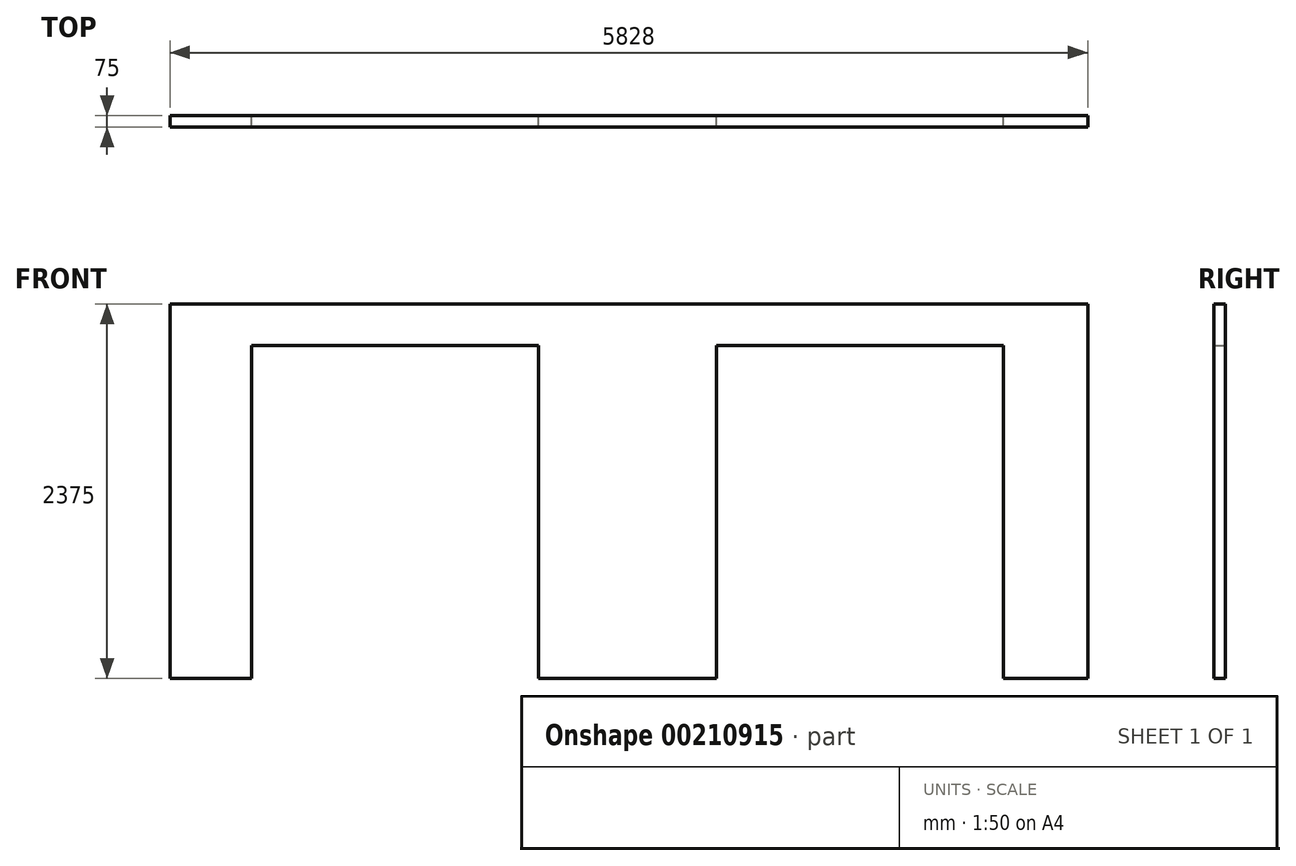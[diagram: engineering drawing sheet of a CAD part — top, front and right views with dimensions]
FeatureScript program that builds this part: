
annotation { "Feature Type Name" : "Feature", "Feature Type Description" : "" }
export const myFeature = defineFeature(function(context is Context, id is Id, definition is map)
    precondition{}
    {
        {
            var Q0;
            Q0=qCreatedBy(makeId("Front.planeOp"),FACE);
            var sketch = newSketch(context, id + "F0", { "sketchPlane" : qUnion([Q0])});
            skLineSegment(sketch, "E0.bottom", {"start": v(0, 0) * mm, "end": v(5828, 0) * mm});
            skLineSegment(sketch, "E0.right", {"start": v(5828, 0) * mm, "end": v(5828, 2375) * mm});
            skLineSegment(sketch, "E1", {"start": v(0, 2375) * mm, "end": v(5828, 2375) * mm});
            skLineSegment(sketch, "E2", {"start": v(0, 0) * mm, "end": v(0, 2375) * mm});
            skLineSegment(sketch, "E3.bottom", {"start": v(518, 0) * mm, "end": v(2340, 0) * mm});
            skLineSegment(sketch, "E3.top", {"start": v(518, 2112) * mm, "end": v(2340, 2112) * mm});
            skLineSegment(sketch, "E3.left", {"start": v(518, 0) * mm, "end": v(518, 2112) * mm});
            skLineSegment(sketch, "E3.right", {"start": v(2340, 0) * mm, "end": v(2340, 2112) * mm});
            skLineSegment(sketch, "E4.bottom", {"start": v(3469, 0) * mm, "end": v(5291, 0) * mm});
            skLineSegment(sketch, "E4.top", {"start": v(3469, 2112) * mm, "end": v(5291, 2112) * mm});
            skLineSegment(sketch, "E4.left", {"start": v(3469, 0) * mm, "end": v(3469, 2112) * mm});
            skLineSegment(sketch, "E4.right", {"start": v(5291, 0) * mm, "end": v(5291, 2112) * mm});
            skSolve(sketch);
        }
        {
            var Q0;
            Q0=makeQuery(id+"F0.imprint","IMPRINT",FACE,{"disambiguationData":[TD([[makeQuery(id+"F0.imprint","IMPRINT",EDGE,{"derivedFrom":sQuery(id+"F0.wireOp",EDGE,"E0.bottom")}),1.0]])]});
            extrude(context, id + "F1", {"entities" : qUnion([Q0]), "depth" : 75 * mm});
        }
    });
